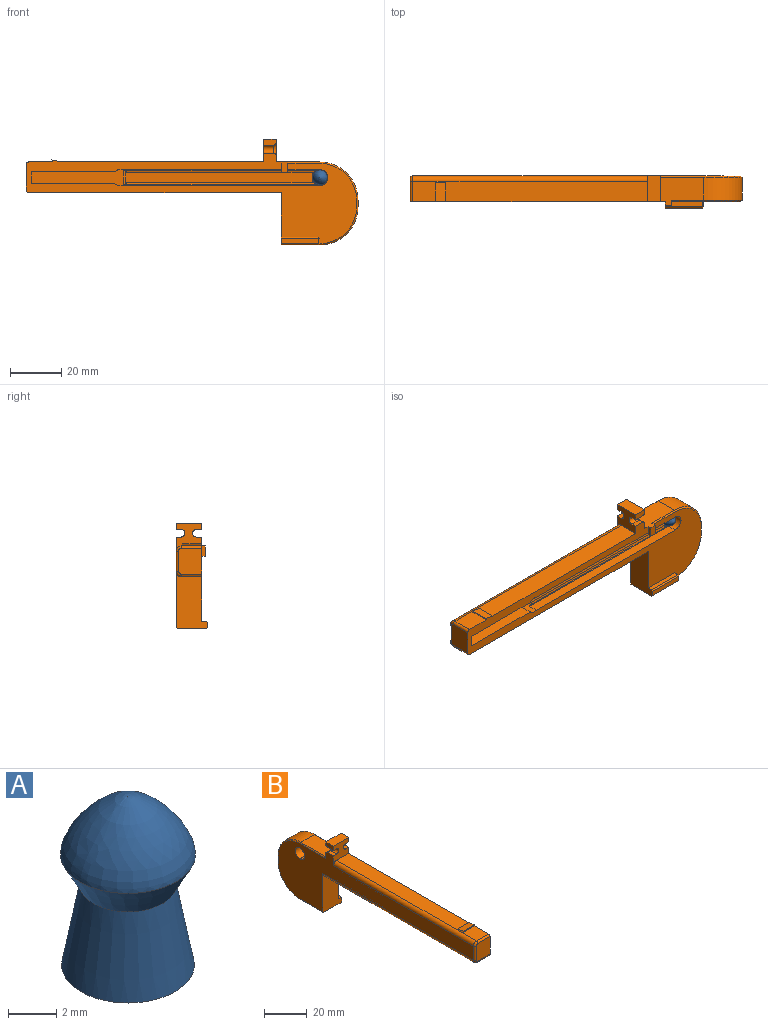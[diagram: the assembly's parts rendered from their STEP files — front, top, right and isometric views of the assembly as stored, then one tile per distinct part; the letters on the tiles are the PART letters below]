
ASSEMBLY  parts=2 mates=1
PART A: 6 faces, bbox 5.6x5.6x8.6 mm
  f0: revolved ~5.6x5.6mm, area 45mm2, adj f1
  f1: cone r=2mm half-angle=28.1deg, axis (0,0,1), area 25.6mm2, adj f0,f2
  f2: cone r=2.75mm half-angle=10.4deg, axis (0,0,-1), area 62.2mm2, adj f1,f5
  f3: cylinder r=1.5mm len=3mm, axis (0,0,-1), area 1.4mm2, adj f4,f5
  f4: plane 3x3mm, normal (0,0,-1), area 7.1mm2, adj f3
  f5: bspline ~5.5x5.5mm, area 29.7mm2, adj f2,f3
PART B: 92 faces, bbox 13.3x130.6x42.1 mm
  f0: plane 5.16x2.66mm, normal (1,0,0), area 12.2mm2, adj f2,f44,f45,f84,f91
  f1: plane 5.16x2.66mm, normal (-1,0,0), area 12.2mm2, adj f2,f44,f45,f82,f86
  f2: plane 10.01x9.51mm, normal (0,1,0), area 50.5mm2, adj f0,f1,f8,f12,f14,f45,f54,f86
  f3: plane 1.94x0.01mm, normal (0,1,0), area 0mm2, adj f28,f41,f47,f74
  f4: plane 82.06x8mm, normal (0,0,1), area 632.9mm2, adj f12,f44,f48,f71,f73
  f5: cylinder r=3.25mm len=8.8mm, axis (1,0,0), area 35mm2, adj f7,f12,f35,f36,f37,f39,f46,f67
  f6: plane 3.61x0.01mm, normal (0,1,0), area 0mm2, adj f12,f30,f42,f47
  f7: plane 3.61x0.01mm, normal (0,1,0), area 0mm2, adj f5,f12,f35,f43
  f8: plane 17x11mm, normal (0,0,1), area 159mm2, adj f2,f11,f12,f18,f23,f24,f54,f66
  f9: cylinder r=3.1mm len=10mm, axis (-1,0,0), area 113.6mm2, adj f12,f14,f27,f28,f29,f30,f31,f32
  f10: plane 22.5x12.5mm, normal (0,-1,0), area 213mm2, adj f12,f14,f16,f20,f21,f25,f49,f50
  f11: plane 4x1.5mm, normal (0,-1,0), area 6mm2, adj f8,f12,f22,f24,f38
  f12: plane 129.66x35.66mm, normal (1,0,0), area 1353.5mm2, adj f2,f4,f5,f6,f7,f8,f9,f10
  f13: plane 9x2.5mm, normal (0,1,0), area 22.5mm2, adj f17,f18,f52,f64
  f14: plane 128.66x35.66mm, normal (-1,0,0), area 1631.2mm2, adj f2,f9,f10,f44,f48,f49,f50,f51
  f15: plane 9.4x8mm, normal (0,0,1), area 75.2mm2, adj f12,f48,f72,f75
  f16: plane 15x11.5mm, normal (0,0,-1), area 171.3mm2, adj f10,f17,f50,f58,f61,f62
  f17: cylinder r=15mm len=15mm, axis (-1,0,0), area 212.1mm2, adj f13,f16,f51,f63
  f18: cylinder r=15mm len=15mm, axis (1,0,0), area 212.1mm2, adj f8,f13,f53,f65
  f19: plane 2x2mm, normal (0,1,0), area 4mm2, adj f12,f56,f59,f61
  f20: plane 14.5x2mm, normal (0,0,1), area 29mm2, adj f10,f12,f55,f56
  f21: plane 14.5x2mm, normal (1,0,0), area 29mm2, adj f10,f55,f58,f59
  f22: plane 2.5x1.5mm, normal (0,0,-1), area 3.7mm2, adj f11,f23,f24,f38
  f23: plane 4x2mm, normal (0,1,0), area 6.1mm2, adj f8,f12,f22,f24,f38,f66
  f24: plane 4x2.5mm, normal (1,0,0), area 10mm2, adj f8,f11,f22,f23
  f25: plane 99x8mm, normal (0,0,-1), area 792mm2, adj f10,f12,f49,f76
  f26: plane 10x9mm, normal (0,-1,0), area 89.6mm2, adj f12,f75,f76,f77,f78,f79
  f27: plane 76x6.2mm, normal (1,0,0), area 456.7mm2, adj f9,f31,f34,f40,f41,f74
  f28: plane 77.61x3.49mm, normal (-0.34,0,0.94), area 228.9mm2, adj f3,f9,f29,f34,f41,f47
  f29: plane 75.15x0.78mm, normal (0.97,0,0.26), area 57.5mm2, adj f9,f28,f30,f47
  f30: plane 77.08x0.38mm, normal (0.83,0,0.55), area 27.4mm2, adj f6,f9,f29,f33,f42,f47
  f31: plane 2.72x0mm, normal (0,-1,0), area 0mm2, adj f9,f27,f36,f40
  f32: plane 3.6x0mm, normal (0,-1,0), area 0mm2, adj f9,f12,f35,f43
  f33: plane 3.6x0mm, normal (0,-1,0), area 0mm2, adj f9,f12,f30,f42
  f34: plane 2.72x0mm, normal (0,-1,0), area 0mm2, adj f9,f27,f28,f41
  f35: plane 77.08x0.38mm, normal (0.83,0,-0.55), area 27.4mm2, adj f5,f7,f9,f32,f37,f43
  f36: plane 77.61x3.49mm, normal (-0.34,0,-0.94), area 228.9mm2, adj f5,f9,f31,f37,f39,f40
  f37: plane 75.15x0.78mm, normal (0.97,0,-0.26), area 57.5mm2, adj f5,f9,f35,f36
  f38: plane 2.5x1mm, normal (-1,0,0), area 2.5mm2, adj f11,f22,f23,f43
  f39: plane 1.94x0.01mm, normal (0,1,0), area 0mm2, adj f5,f36,f40,f74
  f40: plane 77x2.72mm, normal (0,0,-1), area 208.7mm2, adj f27,f31,f36,f39,f74
  f41: plane 77x2.72mm, normal (0,0,1), area 208.7mm2, adj f3,f27,f28,f34,f74
  f42: plane 77x3.6mm, normal (0,0,1), area 277.2mm2, adj f6,f12,f30,f33
  f43: plane 77x3.6mm, normal (0,0,-1), area 277.2mm2, adj f7,f12,f32,f35,f38
  f44: plane 11x10mm, normal (0,-1,0), area 71.8mm2, adj f0,f1,f4,f12,f14,f45,f48,f80
  f45: plane 10x5mm, normal (0,0,1), area 50mm2, adj f0,f1,f2,f44
  f46: plane 36x6.5mm, normal (1,0,0), area 167.1mm2, adj f5,f47,f67,f68,f69,f74
  f47: cylinder r=3.25mm len=8.8mm, axis (1,0,0), area 35mm2, adj f3,f6,f12,f28,f29,f30,f46,f69
  f48: cylinder r=2mm len=92mm, axis (0,1,0), area 289mm2, adj f4,f14,f15,f44,f70,f77
  f49: cylinder r=2mm len=99mm, axis (0,-1,0), area 311mm2, adj f10,f14,f25,f78
  f50: plane 15x0.5mm, normal (-0.71,0,-0.71), area 10.6mm2, adj f10,f14,f16,f51
  f51: cone r=14.5mm half-angle=45deg, axis (1,0,0), area 16.4mm2, adj f14,f17,f50,f52
  f52: plane 2.5x0.5mm, normal (-0.71,0.71,0), area 1.8mm2, adj f13,f14,f51,f53
  f53: cone r=14.5mm half-angle=45deg, axis (1,0,0), area 16.4mm2, adj f14,f18,f52,f54
  f54: plane 17x0.5mm, normal (-0.71,0,0.71), area 12mm2, adj f2,f8,f14,f53
  f55: plane 14.5x0.5mm, normal (0.71,0,0.71), area 10.3mm2, adj f10,f20,f21,f57
  f56: plane 2x0.5mm, normal (0,0.71,0.71), area 1.4mm2, adj f12,f19,f20,f57
  f57: plane 0.5x0.5mm, normal (0.58,0.58,0.58), area 0.2mm2, adj f55,f56,f59
  f58: plane 14.5x0.5mm, normal (0.71,0,-0.71), area 10.3mm2, adj f10,f16,f21,f60
  f59: plane 2x0.5mm, normal (0.71,0.71,0), area 1.4mm2, adj f19,f21,f57,f60
  f60: plane 0.5x0.5mm, normal (0.58,0.58,-0.58), area 0.2mm2, adj f58,f59,f61
  f61: plane 2.5x0.5mm, normal (0,0.71,-0.71), area 1.6mm2, adj f16,f19,f60,f62
  f62: plane 0.5x0.5mm, normal (0.71,0,-0.71), area 0.2mm2, adj f16,f61,f63
  f63: cone r=14.5mm half-angle=45deg, axis (-1,0,0), area 16.4mm2, adj f12,f17,f62,f64
  f64: plane 2.5x0.5mm, normal (0.71,0.71,0), area 1.8mm2, adj f12,f13,f63,f65
  f65: cone r=14.5mm half-angle=45deg, axis (-1,0,0), area 16.4mm2, adj f12,f18,f64,f66
  f66: plane 12.5x0.5mm, normal (0.71,0,0.71), area 8.8mm2, adj f8,f12,f23,f65
  f67: plane 32.65x8.8mm, normal (0,0,-1), area 287.4mm2, adj f5,f12,f46,f68
  f68: plane 8.8x4.5mm, normal (0,1,0), area 39.6mm2, adj f12,f46,f67,f69
  f69: plane 32.65x8.8mm, normal (0,0,1), area 287.4mm2, adj f12,f46,f47,f68
  f70: plane 0.6x0.12mm, normal (-1,0,0), area 0mm2, adj f48,f72,f73
  f71: plane 7.4x4mm, normal (0,0.2,0.98), area 30.2mm2, adj f4,f12,f72,f73
  f72: plane 8x0.8mm, normal (0,-0.89,-0.45), area 6.9mm2, adj f12,f15,f70,f71,f73
  f73: plane 4x0.8mm, normal (-0.71,0.14,0.69), area 2mm2, adj f4,f70,f71,f72
  f74: plane 6.2x1mm, normal (0.78,0.62,0), area 7.9mm2, adj f3,f27,f39,f40,f41,f46
  f75: cylinder r=1mm len=8mm, axis (-1,0,0), area 12.6mm2, adj f12,f15,f26,f77
  f76: cylinder r=1mm len=8mm, axis (-1,0,0), area 12.6mm2, adj f12,f25,f26,f78
  f77: torus R=1mm, axis (0,-1,0), area 4mm2, adj f26,f48,f75,f79
  f78: torus R=1mm, axis (0,-1,0), area 4mm2, adj f26,f49,f76,f79
  f79: cylinder r=1mm len=8mm, axis (0,0,1), area 12.6mm2, adj f14,f26,f77,f78
  f80: cylinder r=1.5mm len=4mm, axis (0,1,0), area 18.8mm2, adj f44,f81,f82,f87
  f81: plane 4x2mm, normal (0,0,1), area 8mm2, adj f14,f44,f80,f88
  f82: plane 4x2mm, normal (0,0,-1), area 8mm2, adj f1,f44,f80,f86
  f83: cylinder r=1.5mm len=4mm, axis (0,1,0), area 18.8mm2, adj f44,f84,f85,f90
  f84: plane 4x2mm, normal (0,0,-1), area 8mm2, adj f0,f44,f83,f91
  f85: plane 4x2mm, normal (0,0,1), area 8mm2, adj f12,f44,f83,f89
  f86: bspline ~2.1x1mm, area 3mm2, adj f1,f2,f82,f87
  f87: bspline ~5x2.5mm, area 9mm2, adj f2,f80,f86,f88
  f88: bspline ~2.1x1mm, area 3mm2, adj f2,f14,f81,f87
  f89: bspline ~2.1x1mm, area 3mm2, adj f2,f12,f85,f90
  f90: bspline ~5x2.5mm, area 9mm2, adj f2,f83,f89,f91
  f91: bspline ~2.1x1mm, area 3mm2, adj f0,f2,f84,f90
PLACE A rot(axis=(0,-0.71,0.71),180deg) t=(15.1,8.82,26.4)mm
PLACE B rot(axis=(0,0,-1),90deg) t=(15,7.5,0)mm
MATE pin_slot A.f3 <-> B.f9  axis (0,1,0) through (15.1,12.5,26.4)mm
